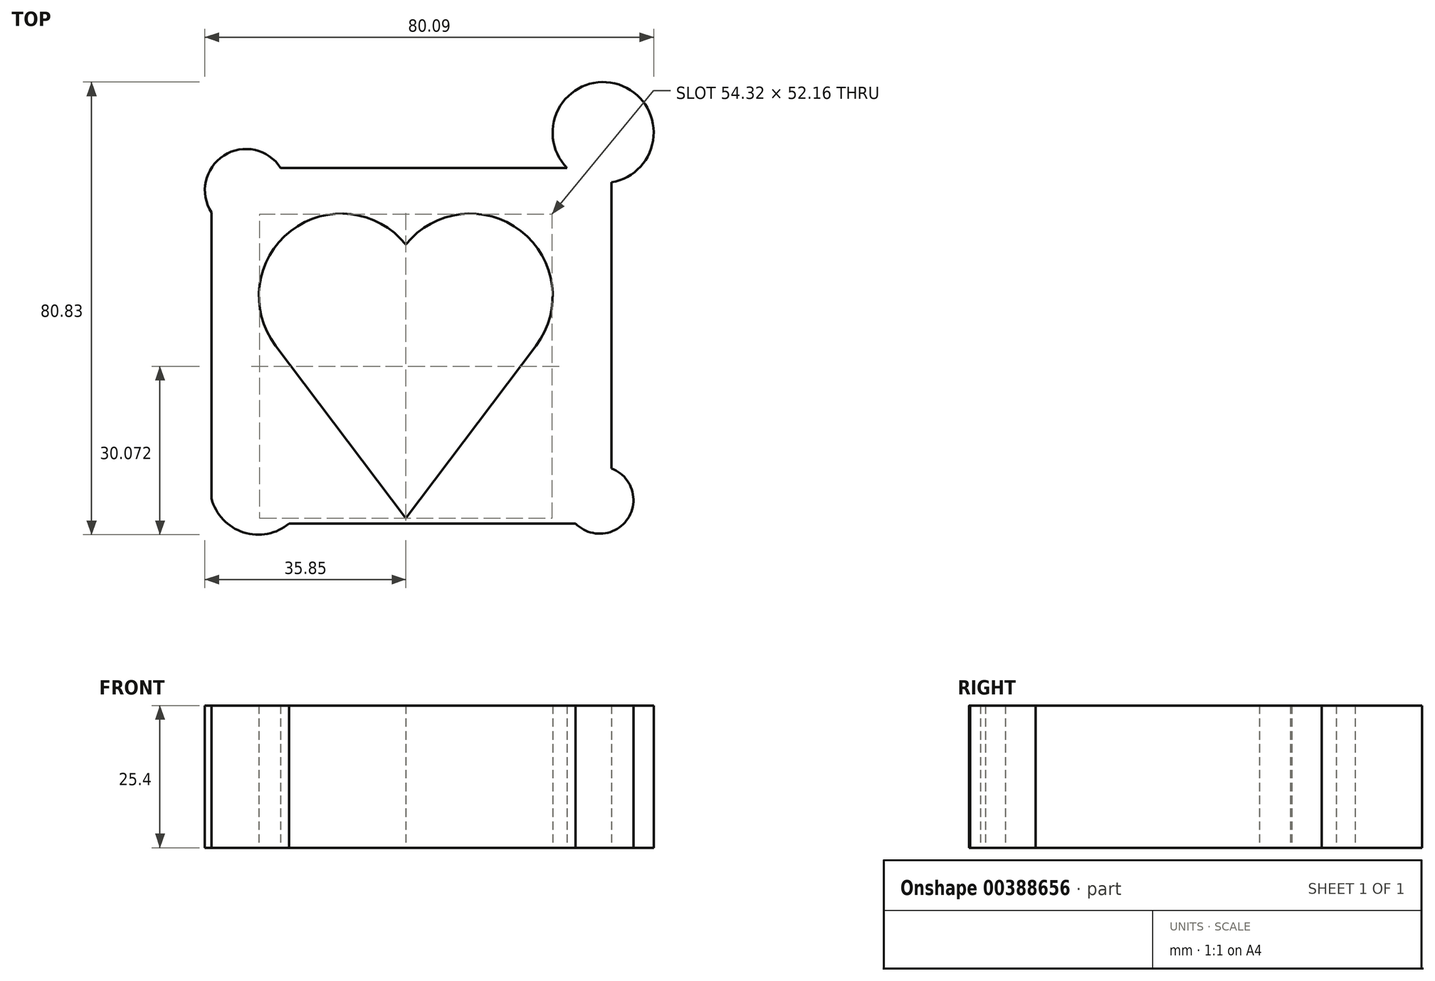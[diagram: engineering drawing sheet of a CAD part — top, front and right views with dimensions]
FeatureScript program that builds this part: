
annotation { "Feature Type Name" : "Feature", "Feature Type Description" : "" }
export const myFeature = defineFeature(function(context is Context, id is Id, definition is map)
    precondition{}
    {
        {
            var Q0;
            Q0=qCreatedBy(makeId("Top.planeOp"),FACE);
            var sketch = newSketch(context, id + "F0", { "sketchPlane" : qUnion([Q0])});
            skEllipse(sketch, "E0", {"center": v(0, -17.78) * mm, "majorRadius": 12.7 * mm, "minorRadius": 4.06 * mm, "majorAxis": v(0, 1)});
            skCircle(sketch, "E1", {"center": v(0, 6.56) * mm, "radius": 4.13 * mm});
            skLineSegment(sketch, "E2", {"start": v(0, -35.06) * mm, "end": v(23.25, -4.2) * mm});
            skLineSegment(sketch, "E3", {"start": v(0, -35.06) * mm, "end": v(-23.25, -4.2) * mm});
            skArc(sketch, "E4", {"start": v(0, 13.84) * mm, "mid": v(-20.52, 16.27) * mm, "end": v(-23.25, -4.2) * mm});
            skArc(sketch, "E5", {"start": v(23.25, -4.2) * mm, "mid": v(20.52, 16.27) * mm, "end": v(0, 13.84) * mm});
            skLineSegment(sketch, "E6", {"start": v(-22.33, 27.54) * mm, "end": v(28.77, 27.54) * mm});
            skLineSegment(sketch, "E7", {"start": v(-20.8, -35.96) * mm, "end": v(30.29, -35.96) * mm});
            skLineSegment(sketch, "E8", {"start": v(-34.68, 19.59) * mm, "end": v(-34.68, -31.5) * mm});
            skLineSegment(sketch, "E9", {"start": v(36.72, 24.95) * mm, "end": v(36.72, -26.15) * mm});
            skArc(sketch, "E10", {"start": v(-22.33, 27.54) * mm, "mid": v(-32.48, 29.74) * mm, "end": v(-34.68, 19.59) * mm});
            skArc(sketch, "E11", {"start": v(36.72, 24.95) * mm, "mid": v(38.01, 42.41) * mm, "end": v(28.77, 27.54) * mm});
            skArc(sketch, "E12", {"start": v(-34.68, -31.5) * mm, "mid": v(-28.97, -37.56) * mm, "end": v(-20.8, -35.96) * mm});
            skArc(sketch, "E13", {"start": v(30.29, -35.96) * mm, "mid": v(39.64, -35.07) * mm, "end": v(36.72, -26.15) * mm});
            skSolve(sketch);
        }
        {
            var Q0;
            Q0=makeQuery(id+"F0.imprint","IMPRINT",FACE,{"disambiguationData":[TD([[makeQuery(id+"F0.imprint","IMPRINT",EDGE,{"derivedFrom":sQuery(id+"F0.wireOp",EDGE,"E2")}),-1.0]])]});
            extrude(context, id + "F1", {"entities" : qUnion([Q0]), "depth" : 25.4 * mm});
        }
    });
